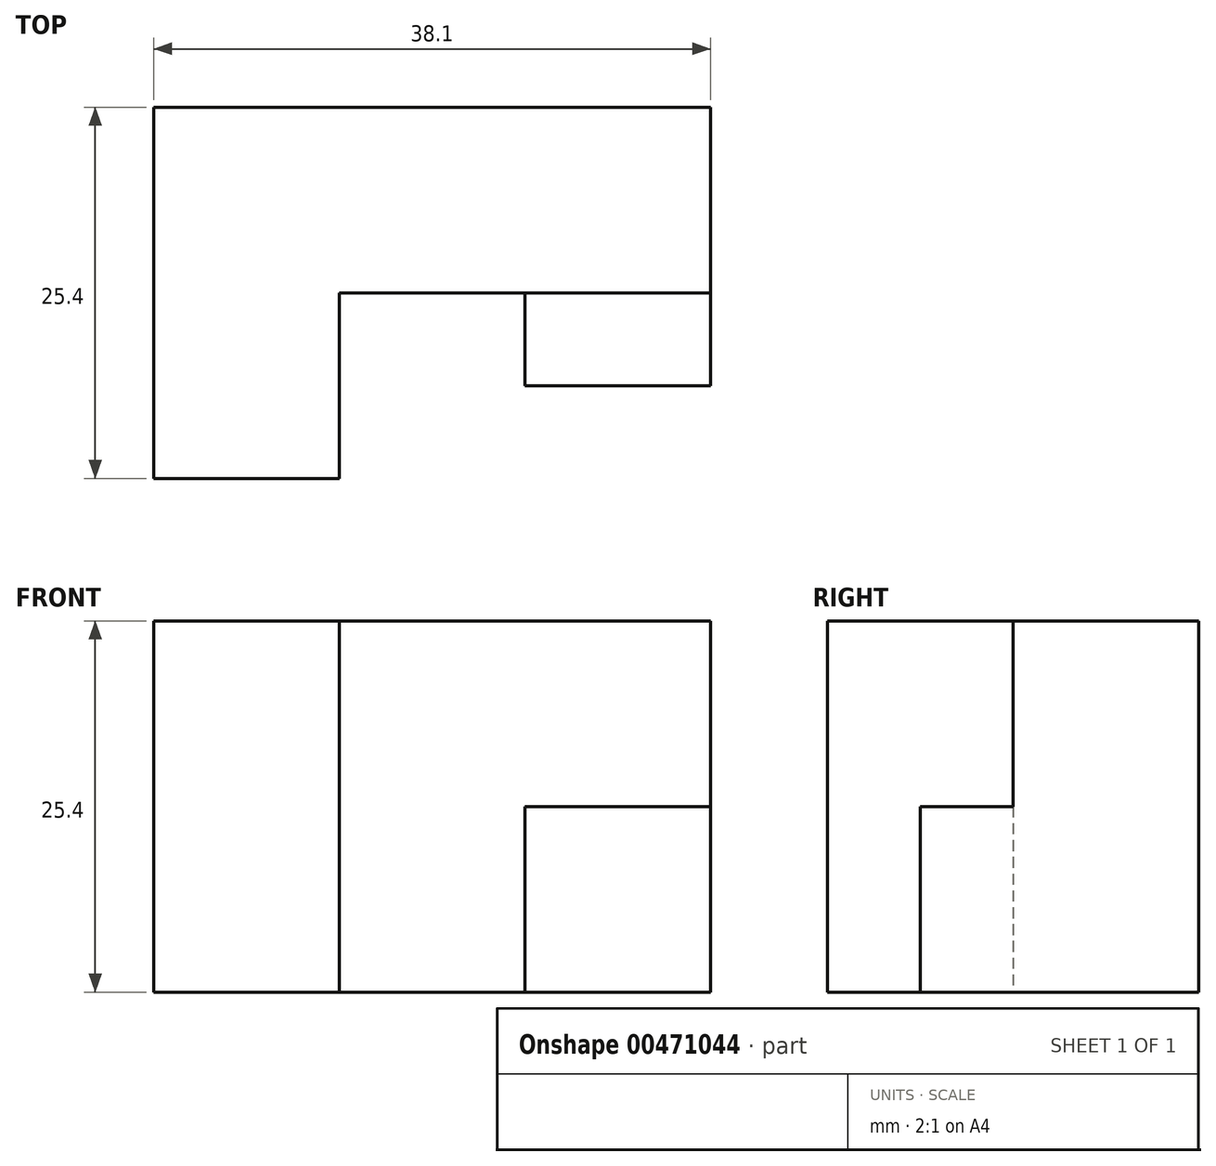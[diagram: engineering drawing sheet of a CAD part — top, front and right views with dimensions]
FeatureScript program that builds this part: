
annotation { "Feature Type Name" : "Feature", "Feature Type Description" : "" }
export const myFeature = defineFeature(function(context is Context, id is Id, definition is map)
    precondition{}
    {
        {
            var Q0;
            Q0=qCreatedBy(makeId("Top.planeOp"),FACE);
            var sketch = newSketch(context, id + "F0", { "sketchPlane" : qUnion([Q0])});
            skLineSegment(sketch, "E0", {"start": v(0, 0) * mm, "end": v(-38.1, 0) * mm});
            skLineSegment(sketch, "E1", {"start": v(-38.1, 0) * mm, "end": v(-38.1, -25.4) * mm});
            skLineSegment(sketch, "E2", {"start": v(-38.1, -25.4) * mm, "end": v(-25.4, -25.4) * mm});
            skLineSegment(sketch, "E3", {"start": v(-25.4, -25.4) * mm, "end": v(-25.4, -12.7) * mm});
            skLineSegment(sketch, "E4", {"start": v(-25.4, -12.7) * mm, "end": v(0, -12.7) * mm});
            skLineSegment(sketch, "E5", {"start": v(0, -12.7) * mm, "end": v(0, 0) * mm});
            skSolve(sketch);
        }
        {
            var Q0;
            Q0=qCreatedBy(makeId("Top.planeOp"),FACE);
            var sketch = newSketch(context, id + "F1", { "sketchPlane" : qUnion([Q0])});
            skLineSegment(sketch, "E6.bottom", {"start": v(0, 0) * mm, "end": v(-12.7, 0) * mm});
            skLineSegment(sketch, "E6.top", {"start": v(0, -19.05) * mm, "end": v(-12.7, -19.05) * mm});
            skLineSegment(sketch, "E6.left", {"start": v(0, 0) * mm, "end": v(0, -19.05) * mm});
            skLineSegment(sketch, "E6.right", {"start": v(-12.7, 0) * mm, "end": v(-12.7, -19.05) * mm});
            skSolve(sketch);
        }
        {
            var Q0;
            Q0=makeQuery(id+"F0.imprint","IMPRINT",FACE,{"disambiguationData":[TD([[makeQuery(id+"F0.imprint","IMPRINT",EDGE,{"derivedFrom":sQuery(id+"F0.wireOp",EDGE,"E0")}),1.0]])]});
            extrude(context, id + "F2", {"entities" : qUnion([Q0]), "depth" : 25.4 * mm});
        }
        {
            var Q0;
            Q0=makeQuery(id+"F1.imprint","IMPRINT",FACE,{"disambiguationData":[TD([[makeQuery(id+"F1.imprint","IMPRINT",EDGE,{"derivedFrom":sQuery(id+"F1.wireOp",EDGE,"E6.bottom")}),1.0]])]});
            extrude(context, id + "F3", {"entities" : qUnion([Q0]), "operationType" : NewBodyOperationType.ADD, "depth" : 12.7 * mm});
        }
    });
